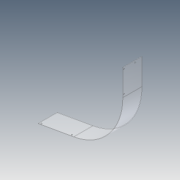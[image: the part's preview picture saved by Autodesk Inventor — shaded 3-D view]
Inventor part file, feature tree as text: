
AUTODESK INVENTOR PART (.ipt)
format: ipt  version: 2012 (Build 160160000, 160)  size: 93,184 bytes
history: native  units: in
note: dims shown in document units (in); Inventor stores cm internally (conversion verified against a paired STEP export)
features: pattern_linear x3, hole x2, extrude x1, sketch x1, reference x1
ambient origin geometry x8: Origin, YZ Plane, XZ Plane, XY Plane, X Axis, Y Axis, Z Axis, Center Point
bodies: Solid1 (feature_tree)
feature tree (8):
  extrude  "Extrusion1"  Depth=0.7874in
  hole  "Hole1"  [1 undecoded]
  pattern_linear  "Rectangular Pattern1"  Count1=2 Spacing1=7.5in
  hole  "Hole2"  [1 undecoded]
  pattern_linear  "Rectangular Pattern2"  [2 undecoded]
  pattern_linear  "Rectangular Pattern3"  [2 undecoded]
  sketch  "Sketch1"  dims[d0=4.625in d1=0.0in d2=0.5in d3=0.3125in d4=0.265in d5=0.75in d6=0.375in d7=0.25in d8=0.5635in d9=1.0in d10=0.8108in d11=0.7874in d13=5.25in d14=0.3125in d15=0.5in d16=0.265in d17=0.75in d18=0.375in d19=0.25in d20=0.5635in d21=1.0in d22=0.8108in d23=0.7874in d25=7.5in d26=0.7874in d28=2.6875in]
  reference  "Reference1"
note: 6 required parameter values undecoded (feature->parameter linkage not recoverable at this tier; creation-order binding heuristic only, values carry confidence <= 0.55)
